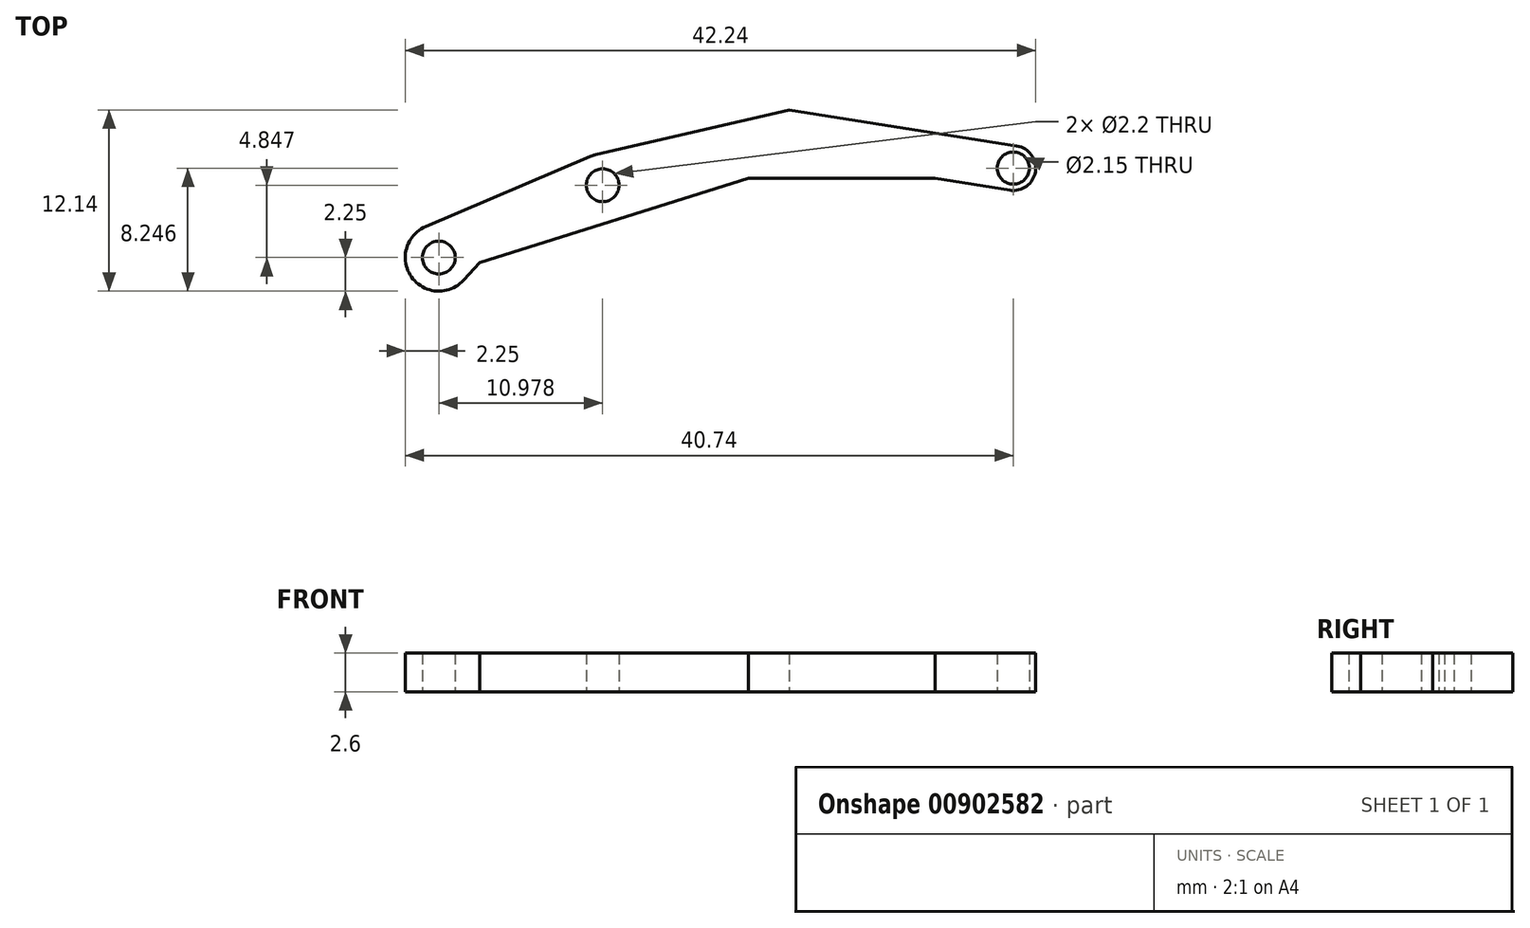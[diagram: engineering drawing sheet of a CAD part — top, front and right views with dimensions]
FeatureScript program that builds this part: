
annotation { "Feature Type Name" : "Feature", "Feature Type Description" : "" }
export const myFeature = defineFeature(function(context is Context, id is Id, definition is map)
    precondition{}
    {
        {
            var Q0;
            Q0=qCreatedBy(makeId("Top.planeOp"),FACE);
            var sketch = newSketch(context, id + "F0", { "sketchPlane" : qUnion([Q0])});
            skCircle(sketch, "E0", {"center": v(-3.92, 2.88) * mm, "radius": 2.1 * mm});
            skCircle(sketch, "E1", {"center": v(-14.9, -1.97) * mm, "radius": 2.25 * mm});
            skCircle(sketch, "E2", {"center": v(23.6, 4.03) * mm, "radius": 1.5 * mm});
            skLineSegment(sketch, "E3", {"start": v(-4.4, 4.92) * mm, "end": v(8.58, 7.92) * mm});
            skLineSegment(sketch, "E4", {"start": v(-4.75, 4.8) * mm, "end": v(-16.02, 0) * mm});
            skLineSegment(sketch, "E5", {"start": v(5.85, 3.33) * mm, "end": v(18.37, 3.33) * mm});
            skCircle(sketch, "E6", {"center": v(23.6, 4.03) * mm, "radius": 1.07 * mm});
            skCircle(sketch, "E7", {"center": v(-3.92, 2.88) * mm, "radius": 1.1 * mm});
            skCircle(sketch, "E8", {"center": v(-14.9, -1.97) * mm, "radius": 1.1 * mm});
            skLineSegment(sketch, "E9", {"start": v(-13.24, -3.49) * mm, "end": v(-12.16, -2.3) * mm});
            skLineSegment(sketch, "E10", {"start": v(-12.16, -2.3) * mm, "end": v(5.85, 3.33) * mm});
            skLineSegment(sketch, "E11", {"start": v(18.37, 3.33) * mm, "end": v(23.36, 2.54) * mm});
            skLineSegment(sketch, "E12", {"start": v(8.58, 7.92) * mm, "end": v(23.82, 5.5) * mm});
            skSolve(sketch);
        }
        {
            var Q0;
            Q0=qSketchRegion(id+"F0",true);
            extrude(context, id + "F1", {"entities" : qUnion([Q0]), "depth" : 2.6 * mm, "offsetDistance" : 25 * mm});
        }
    });
